# Revit family: Serene_T&T_Window_C_Custom
name_source: partatom
category: Windows
revit_build: Autodesk Revit 2014 (Build: 20130308_1515(x64)
units: mm (PartAtom-declared; Revit-internal decimal feet)

## types (1)
- Serene_T&T_Window_C_Custom
    Area Glazing Fixed Panel = 0.48 m²
    Area Glazing Sash = 0.3 m²
    Centered In Wall = Yes
    Custom SHGC Value = 0
    Custom Sash Width = 522 mm  [stored 1.7126 ft]
    Custom U Value = 0
    Custom Windload = 1000 mm  [stored 3.28084 ft]
    Custom Window Exterior Offset = 0 mm  [stored 0 ft]
    Custom Window Height = 890 mm  [stored 2.91995 ft]
    Custom Window Width = 1790 mm  [stored 5.8727 ft]
    DG Gasket Finish = Double Glazing Gasket Material
    DG Gasket Tickness = 12 mm  [stored 0.0393701 ft]
    DG Thickness Calc = 4 mm  [stored 0.0131234 ft]
    Default Sill Height = 800 mm  [stored 2.62467 ft]
    Description = Tilt and turn window, Type C custom
    Fixed Panel Height = 810 mm  [stored 2.65748 ft]
    Fixed Panel Width = 611 mm
    Frame Thickness = 52 mm
    Frame Width = 62 mm
    Height = 890 mm  [stored 2.91995 ft]
    Length Mullion = 810 mm  [stored 2.65748 ft]
    Limit Fixed Pane Height Min = 200 mm  [stored 0.656168 ft]
    Limit Fixed Panel Width Max = 1800 mm
    Limit Fixed Panel Width Min = 200 mm  [stored 0.656168 ft]
    Limit Sash Height Max = 1500 mm  [stored 4.92126 ft]
    Limit Sash Height Min = 300 mm  [stored 0.984252 ft]
    Limit Sash Width Max = 700 mm  [stored 2.29659 ft]
    Limit Sash Width Min = 300 mm  [stored 0.984252 ft]
    Limit Window Height Max = 1568 mm
    Limit Window Height Min = 368 mm
    Limit Window Width Max = 2979 mm
    Limit Window Width Min = 1379 mm
    Manufacturer = Crealco
    Max Pane Area = 0.48 m²
    Max System DG One Piece Thickness = 4 mm  [stored 0.0131234 ft]
    Max System DG Unit Thickness = 20 mm  [stored 0.0656168 ft]
    Model = Serene
    Mullion Side Spacing = 528 mm  [stored 1.73228 ft]
    Sash Edge Gap = 34 mm
    Sash Frame Gasket = 3 mm  [stored 0.00984252 ft]
    Sash Height = 822 mm  [stored 2.69685 ft]
    Sash Overlap = 28 mm
    Sash Width = 522 mm  [stored 1.7126 ft]
    URL = http://www.crealco.co.za
    Wall Closure = By host
    Width = 1790 mm  [stored 5.8727 ft]
    Windload Design = 1000 mm  [stored 3.28084 ft]

note: [stored X ft] marks values corroborated as IEEE doubles in the binary element streams (Revit-internal decimal feet)

## geometry (parser evidence)
native form markers: Sweep x31
no freeform markers — native parametric forms only
